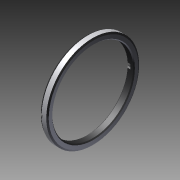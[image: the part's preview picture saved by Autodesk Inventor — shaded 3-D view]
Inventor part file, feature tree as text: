
AUTODESK INVENTOR PART (.ipt)
format: ipt  version: 2012 SP2 (Build 160219200, 219)  size: 122,880 bytes
history: native  units: mm
features: chamfer x1, imported_body x1
ambient origin geometry x8: Origin, YZ Plane, XZ Plane, XY Plane, X Axis, Y Axis, Z Axis, Center Point
feature tree (2):
  chamfer  "Chamfer2"  [1 undecoded]
  imported_body  "Base1"
note: 1 required parameter value undecoded (feature->parameter linkage not recoverable at this tier; creation-order binding heuristic only, values carry confidence <= 0.55)
